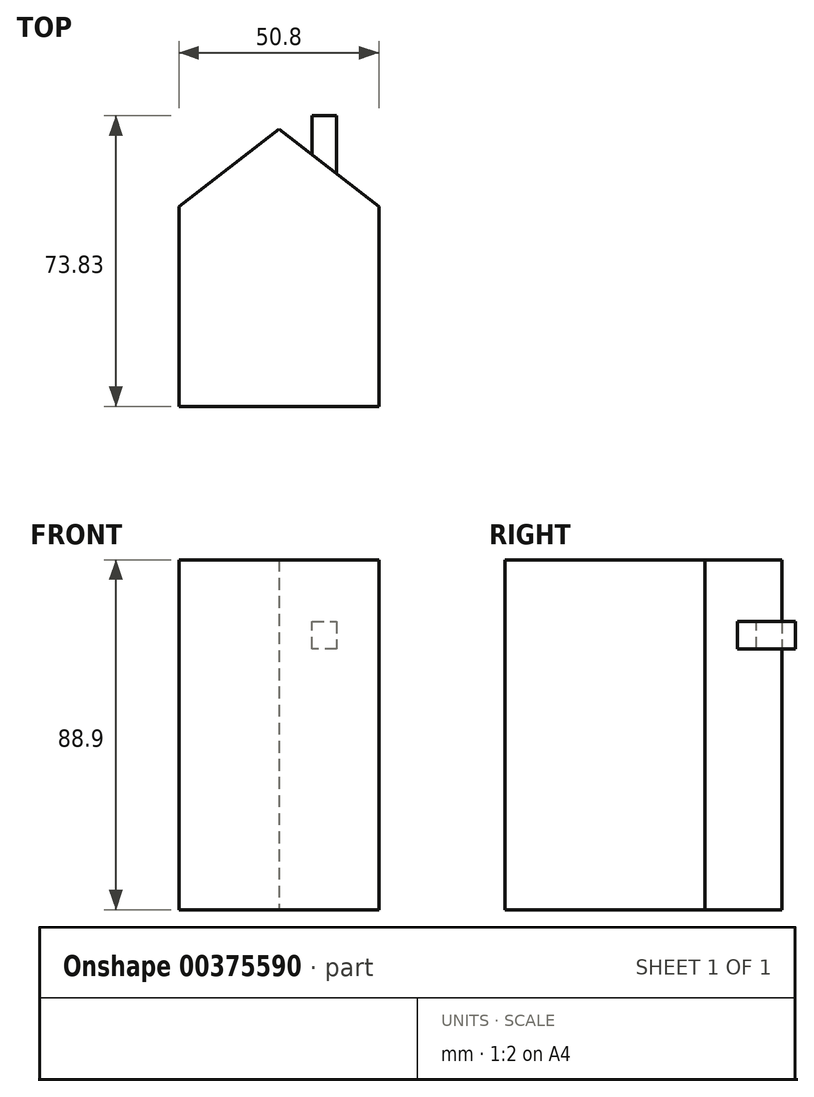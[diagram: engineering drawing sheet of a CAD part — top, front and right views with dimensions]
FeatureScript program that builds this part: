
annotation { "Feature Type Name" : "Feature", "Feature Type Description" : "" }
export const myFeature = defineFeature(function(context is Context, id is Id, definition is map)
    precondition{}
    {
        {
            var Q0;
            Q0=qCreatedBy(makeId("Top.planeOp"),FACE);
            var sketch = newSketch(context, id + "F0", { "sketchPlane" : qUnion([Q0])});
            skLineSegment(sketch, "E0.top", {"start": v(-33.82, -30.65) * mm, "end": v(16.98, -30.65) * mm});
            skLineSegment(sketch, "E0.left", {"start": v(-33.82, 20.15) * mm, "end": v(-33.82, -30.65) * mm});
            skLineSegment(sketch, "E0.right", {"start": v(16.98, 20.15) * mm, "end": v(16.98, -30.65) * mm});
            skLineSegment(sketch, "E1", {"start": v(-33.82, 20.15) * mm, "end": v(-8.42, 39.77) * mm});
            skPoint(sketch, "E1.endSnap0", {"position": v(-8.42, 20.15) * mm});
            skLineSegment(sketch, "E2", {"start": v(-8.42, 39.77) * mm, "end": v(16.98, 20.15) * mm});
            skSolve(sketch);
        }
        {
            var Q0;
            Q0=makeQuery(id+"F0.imprint","IMPRINT",FACE,{"disambiguationData":[TD([[makeQuery(id+"F0.imprint","IMPRINT",EDGE,{"derivedFrom":sQuery(id+"F0.wireOp",EDGE,"E0.top")}),1.0]])]});
            extrude(context, id + "F1", {"entities" : qUnion([Q0]), "depth" : 88.9 * mm});
        }
        {
            var Q0;
            Q0=qCreatedBy(makeId("Front.planeOp"),FACE);
            var sketch = newSketch(context, id + "F2", { "sketchPlane" : qUnion([Q0])});
            skLineSegment(sketch, "E3", {"start": v(0, 73.22) * mm, "end": v(0, 66.3) * mm});
            skLineSegment(sketch, "E4", {"start": v(0, 66.3) * mm, "end": v(6.29, 66.3) * mm});
            skLineSegment(sketch, "E5", {"start": v(6.29, 66.3) * mm, "end": v(6.29, 73.22) * mm});
            skLineSegment(sketch, "E6", {"start": v(6.29, 73.22) * mm, "end": v(0, 73.22) * mm});
            skSolve(sketch);
        }
        {
            var Q0;
            Q0 = qSketchRegion(id + "F2", true);
            extrude(context, id + "F3", {"entities" : qUnion([Q0]), "operationType" : NewBodyOperationType.ADD, "oppositeDirection" : true, "depth" : 43.18 * mm});
        }
    });
